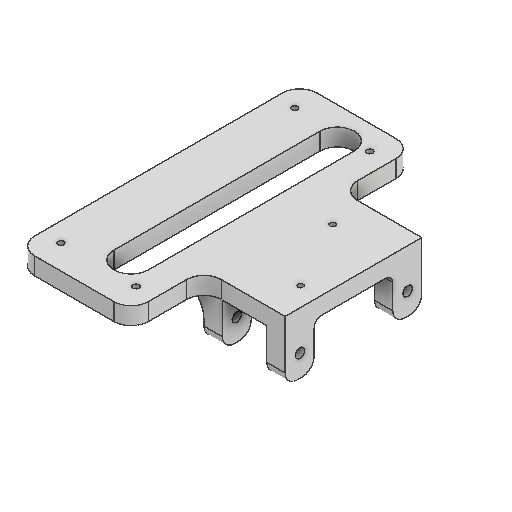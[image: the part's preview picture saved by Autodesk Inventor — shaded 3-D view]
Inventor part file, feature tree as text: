
AUTODESK INVENTOR PART (.ipt)
format: ipt  version: 2025 (Build 290162000, 162)  size: 330,752 bytes
history: native  units: mm
features: extrude x7, sketch x7, projected_geometry x6, fillet x5, other x3, reference x2
ambient origin geometry x8: Origin, YZ Plane, XZ Plane, XY Plane, X Axis, Y Axis, Z Axis, Center Point
bodies: Solid1 (feature_tree)
feature tree (30):
  extrude  "Extrusion1"  Depth=10.0mm TaperAngle=0.0deg
  extrude  "Extrusion2"  Depth=43.5mm
  extrude  "Extrusion3"  Depth=25.8mm
  extrude  "Extrusion5"  Depth=5.5mm
  fillet  "Fillet4"  [1 undecoded]
  extrude  "Extrusion6"  TaperAngle=0.0deg  [1 undecoded]
  fillet  "Fillet5"  Radius=4.0mm
  fillet  "Fillet6"  [1 undecoded]
  extrude  "Extrusion7"  Depth=10.0mm
  fillet  "Fillet7"  Radius=10.0mm
  fillet  "Fillet8"  Radius=10.0mm
  extrude  "Extrusion4"  Depth=1.0mm
  sketch  "Sketch1"  dims[d0=3.5mm d1=10.0mm d2=0.0mm]
  sketch  "Sketch2"  dims[d3=135.5mm d4=43.5mm]
  reference  "Reference1"
  reference  "Reference2"
  sketch  "Sketch3"  dims[d5=0.0mm d6=0.0mm d7=25.8mm]
  projected_geometry  "Projected Loop1"
  sketch  "Sketch4"  dims[d8=25.4mm d9=0.0mm d13=5.5mm d14=0.0mm d15=0.0mm]
  projected_geometry  "Projected Loop2"
  projected_geometry  "Projected Loop3"
  sketch  "Sketch5"  dims[d16=5.5mm d17=0.0mm d18=0.0mm d19=4.0mm d20=0.0mm d21=0.0mm]
  projected_geometry  "Projected Loop4"
  projected_geometry  "Projected Loop5"
  sketch  "Sketch6"  dims[d22=10.0mm d23=15.0mm d24=10.0mm d25=10.0mm]
  projected_geometry  "Projected Loop6"
  sketch  "Sketch7"  dims[d26=10.0mm d27=0.0mm d28=7.0mm d29=1.0mm]
  other  "<userpath>\Desktop\puppycat\singleSwingarmV2.iam"
  other  "singleSwingarmV2.iam"
  other  "50W 2Ohm Power Resistor:1"
note: 3 required parameter values undecoded (feature->parameter linkage not recoverable at this tier; creation-order binding heuristic only, values carry confidence <= 0.55)
